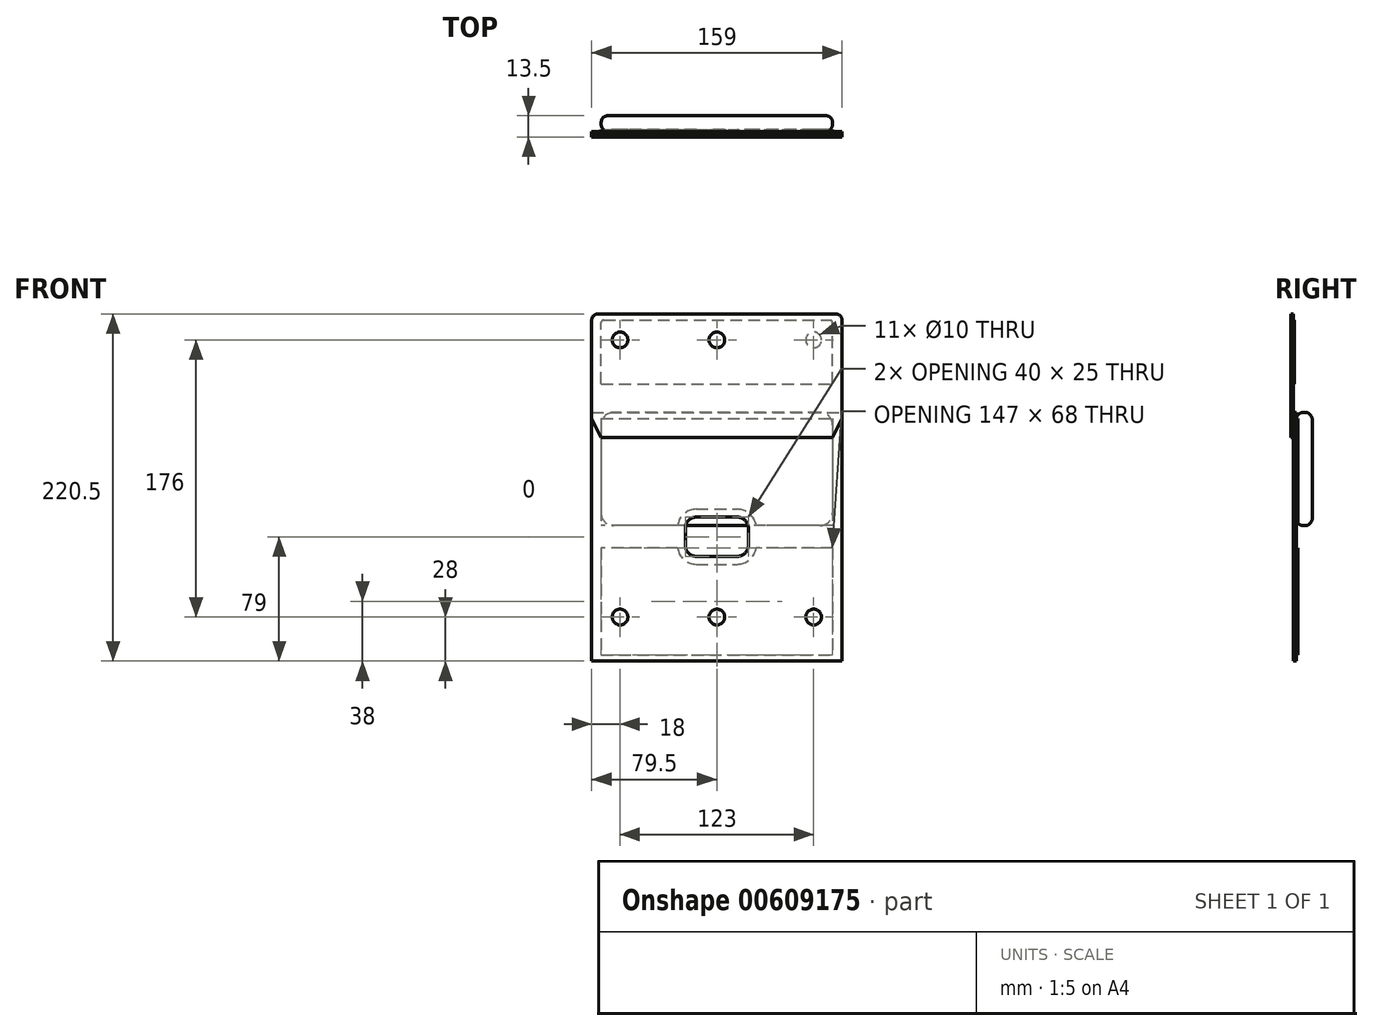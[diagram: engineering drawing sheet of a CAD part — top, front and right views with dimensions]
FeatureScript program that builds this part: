
annotation { "Feature Type Name" : "Feature", "Feature Type Description" : "" }
export const myFeature = defineFeature(function(context is Context, id is Id, definition is map)
    precondition{}
    {
        {
            var Q0;
            Q0=qCreatedBy(makeId("Front.planeOp"),FACE);
            var sketch = newSketch(context, id + "F0", { "sketchPlane" : qUnion([Q0])});
            skLineSegment(sketch, "E0.bottom", {"start": v(65.5, 36) * mm, "end": v(-65.5, 36) * mm});
            skLineSegment(sketch, "E0.top", {"start": v(65.5, -36) * mm, "end": v(-65.5, -36) * mm});
            skLineSegment(sketch, "E0.left", {"start": v(73.5, 28) * mm, "end": v(73.5, -28) * mm});
            skLineSegment(sketch, "E0.right", {"start": v(-73.5, 28) * mm, "end": v(-73.5, -28) * mm});
            skPoint(sketch, "E0.middle", {"position": v(0, 0) * mm});
            skPoint(sketch, "E1.visualSharp", {"position": v(-73.5, 36) * mm});
            skArc(sketch, "E1.filletArc", {"start": v(-65.5, 36) * mm, "mid": v(-71.16, 33.66) * mm, "end": v(-73.5, 28) * mm});
            skPoint(sketch, "E2.visualSharp", {"position": v(-73.5, -36) * mm});
            skArc(sketch, "E2.filletArc", {"start": v(-73.5, -28) * mm, "mid": v(-71.16, -33.66) * mm, "end": v(-65.5, -36) * mm});
            skPoint(sketch, "E3.visualSharp", {"position": v(73.5, -36) * mm});
            skArc(sketch, "E3.filletArc", {"start": v(65.5, -36) * mm, "mid": v(71.16, -33.66) * mm, "end": v(73.5, -28) * mm});
            skPoint(sketch, "E4.visualSharp", {"position": v(73.5, 36) * mm});
            skArc(sketch, "E4.filletArc", {"start": v(73.5, 28) * mm, "mid": v(71.16, 33.66) * mm, "end": v(65.5, 36) * mm});
            skSolve(sketch);
        }
        {
            var Q0;
            Q0=makeQuery(id+"F0.imprint","IMPRINT",FACE,{"disambiguationData":[TD([[makeQuery(id+"F0.imprint","IMPRINT",EDGE,{"derivedFrom":sQuery(id+"F0.wireOp",EDGE,"E0.bottom")}),1.0]])]});
            extrude(context, id + "F1", {"entities" : qUnion([Q0]), "endBound" : BoundingType.SYMMETRIC, "depth" : 10 * mm, "offsetDistance" : 25 * mm});
        }
        {
            var Q0;
            Q0=makeQuery(id+"F1.opExtrude","CAP_FACE",FACE,{"disambiguationData":[OSD([sQuery(id+"F0.wireOp",EDGE,"E0.bottom"),sQuery(id+"F0.wireOp",EDGE,"E0.top"),sQuery(id+"F0.wireOp",EDGE,"E0.left"),sQuery(id+"F0.wireOp",EDGE,"E0.right"),sQuery(id+"F0.wireOp",EDGE,"E1.filletArc"),sQuery(id+"F0.wireOp",EDGE,"E2.filletArc"),sQuery(id+"F0.wireOp",EDGE,"E3.filletArc"),sQuery(id+"F0.wireOp",EDGE,"E4.filletArc")])],"isStart":false});
            var Q1;
            Q1=makeQuery(id+"F1.opExtrude","CAP_FACE",FACE,{"disambiguationData":[OSD([sQuery(id+"F0.wireOp",EDGE,"E0.bottom"),sQuery(id+"F0.wireOp",EDGE,"E0.top"),sQuery(id+"F0.wireOp",EDGE,"E0.left"),sQuery(id+"F0.wireOp",EDGE,"E0.right"),sQuery(id+"F0.wireOp",EDGE,"E1.filletArc"),sQuery(id+"F0.wireOp",EDGE,"E2.filletArc"),sQuery(id+"F0.wireOp",EDGE,"E3.filletArc"),sQuery(id+"F0.wireOp",EDGE,"E4.filletArc")])],"isStart":true});
            fillet(context, id + "F2", {"entities" : qUnion([Q0, Q1]), "radius" : 4.5 * mm, "tangentPropagation" : true, "allowEdgeOverflow" : false});
        }
        {
            var Q0;
            Q0=makeQuery(id+"F1.opExtrude","CAP_FACE",FACE,{"disambiguationData":[OSD([sQuery(id+"F0.wireOp",EDGE,"E0.bottom"),sQuery(id+"F0.wireOp",EDGE,"E0.top"),sQuery(id+"F0.wireOp",EDGE,"E0.left"),sQuery(id+"F0.wireOp",EDGE,"E0.right"),sQuery(id+"F0.wireOp",EDGE,"E1.filletArc"),sQuery(id+"F0.wireOp",EDGE,"E2.filletArc"),sQuery(id+"F0.wireOp",EDGE,"E3.filletArc"),sQuery(id+"F0.wireOp",EDGE,"E4.filletArc")])],"isStart":false});
            var sketch = newSketch(context, id + "F3", { "sketchPlane" : qUnion([Q0])});
            skLineSegment(sketch, "E5.0", {"start": v(-65.5, 36) * mm, "end": v(65.5, 36) * mm});
            skLineSegment(sketch, "E6.0", {"start": v(-73.5, -122) * mm, "end": v(-73.5, 36) * mm, "construction": true});
            skLineSegment(sketch, "E7.0", {"start": v(73.5, 36) * mm, "end": v(73.5, -122) * mm, "construction": true});
            skLineSegment(sketch, "E8.0", {"start": v(73.5, -36) * mm, "end": v(24.9, -36) * mm});
            skPoint(sketch, "E9.orphan", {"position": v(-73.5, 28) * mm});
            skPoint(sketch, "E10.orphan", {"position": v(-65.5, 36) * mm});
            skPoint(sketch, "E11.orphan", {"position": v(73.5, 28) * mm});
            skPoint(sketch, "E12.orphan", {"position": v(65.5, 36) * mm});
            skLineSegment(sketch, "E13", {"start": v(-20, -43) * mm, "end": v(20, -43) * mm, "construction": true});
            skLineSegment(sketch, "E14.MirrorCS", {"start": v(-79.5, -122) * mm, "end": v(79.5, -122) * mm, "construction": true});
            skPoint(sketch, "E15.orphan", {"position": v(-73.5, -28) * mm});
            skPoint(sketch, "E16.orphan", {"position": v(73.5, -28) * mm});
            skLineSegment(sketch, "E17", {"start": v(-73.5, 32) * mm, "end": v(73.5, 32) * mm});
            skLineSegment(sketch, "E18", {"start": v(-79.5, 36) * mm, "end": v(-79.5, -122) * mm});
            skLineSegment(sketch, "E19.MirrorCS", {"start": v(79.5, 36) * mm, "end": v(79.5, -122) * mm});
            skPoint(sketch, "E20.orphan", {"position": v(79.5, 36) * mm});
            skPoint(sketch, "E21.orphan", {"position": v(0, 32) * mm});
            skPoint(sketch, "E22.orphan", {"position": v(-65.5, -36) * mm});
            skPoint(sketch, "E23.orphan", {"position": v(65.5, -36) * mm});
            skLineSegment(sketch, "E24", {"start": v(-73.5, 32) * mm, "end": v(-73.5, -36) * mm});
            skLineSegment(sketch, "E25", {"start": v(73.5, 32) * mm, "end": v(73.5, -36) * mm});
            skLineSegment(sketch, "E26.trimOffspring", {"start": v(-24.9, -36) * mm, "end": v(-73.5, -36) * mm});
            skLineSegment(sketch, "E27.MirrorCS", {"start": v(-24.9, -50) * mm, "end": v(-73.5, -50) * mm});
            skLineSegment(sketch, "E28.MirrorCS", {"start": v(-73.5, 36) * mm, "end": v(-73.5, -122) * mm, "construction": true});
            skLineSegment(sketch, "E29.MirrorCS", {"start": v(-73.5, -118) * mm, "end": v(73.5, -118) * mm});
            skLineSegment(sketch, "E30.MirrorCS", {"start": v(73.5, -50) * mm, "end": v(24.9, -50) * mm});
            skLineSegment(sketch, "E31", {"start": v(-73.5, -50) * mm, "end": v(-73.5, -118) * mm});
            skLineSegment(sketch, "E32", {"start": v(73.5, -50) * mm, "end": v(73.5, -118) * mm});
            skCircle(sketch, "E33", {"center": v(61.5, -94) * mm, "radius": 5 * mm});
            skCircle(sketch, "E34.MirrorC", {"center": v(-61.5, -94) * mm, "radius": 5 * mm});
            skLineSegment(sketch, "E35", {"start": v(79.5, 36) * mm, "end": v(-79.5, 36) * mm});
            skPoint(sketch, "E36.orphan", {"position": v(-79.5, 36) * mm});
            skLineSegment(sketch, "E37.MirrorCS", {"start": v(79.5, -122) * mm, "end": v(-79.5, -122) * mm});
            skLineSegment(sketch, "E38.bottom", {"start": v(-13, -30.5) * mm, "end": v(13, -30.5) * mm});
            skLineSegment(sketch, "E38.top", {"start": v(-13, -55.5) * mm, "end": v(13, -55.5) * mm});
            skLineSegment(sketch, "E38.left", {"start": v(-20, -37.5) * mm, "end": v(-20, -48.5) * mm});
            skLineSegment(sketch, "E38.right", {"start": v(20, -37.5) * mm, "end": v(20, -48.5) * mm});
            skPoint(sketch, "E39.visualSharp", {"position": v(-20, -30.5) * mm});
            skArc(sketch, "E39.filletArc", {"start": v(-13, -30.5) * mm, "mid": v(-17.95, -32.55) * mm, "end": v(-20, -37.5) * mm});
            skPoint(sketch, "E40.visualSharp", {"position": v(-20, -55.5) * mm});
            skArc(sketch, "E40.filletArc", {"start": v(-20, -48.5) * mm, "mid": v(-17.95, -53.45) * mm, "end": v(-13, -55.5) * mm});
            skPoint(sketch, "E41.visualSharp", {"position": v(20, -55.5) * mm});
            skArc(sketch, "E41.filletArc", {"start": v(13, -55.5) * mm, "mid": v(17.95, -53.45) * mm, "end": v(20, -48.5) * mm});
            skPoint(sketch, "E42.visualSharp", {"position": v(20, -30.5) * mm});
            skArc(sketch, "E42.filletArc", {"start": v(20, -37.5) * mm, "mid": v(17.95, -32.55) * mm, "end": v(13, -30.5) * mm});
            skArc(sketch, "E43", {"start": v(-13, -25.5) * mm, "mid": v(-20.94, -28.5) * mm, "end": v(-24.9, -36) * mm});
            skLineSegment(sketch, "E44", {"start": v(-13, -25.5) * mm, "end": v(13, -25.5) * mm});
            skPoint(sketch, "E45.orphan", {"position": v(-22.7, -36) * mm});
            skPoint(sketch, "E46.orphan", {"position": v(22.7, -36) * mm});
            skArc(sketch, "E47.MirrorCS", {"start": v(13, -25.5) * mm, "mid": v(20.94, -28.5) * mm, "end": v(24.9, -36) * mm});
            skArc(sketch, "E48.MirrorCS", {"start": v(-13, -60.5) * mm, "mid": v(-20.94, -57.5) * mm, "end": v(-24.9, -50) * mm});
            skLineSegment(sketch, "E49.MirrorCS", {"start": v(-13, -60.5) * mm, "end": v(13, -60.5) * mm});
            skArc(sketch, "E50.MirrorCS", {"start": v(13, -60.5) * mm, "mid": v(20.94, -57.5) * mm, "end": v(24.9, -50) * mm});
            skPoint(sketch, "E51.orphan", {"position": v(-22.7, -50) * mm});
            skPoint(sketch, "E52.orphan", {"position": v(22.7, -50) * mm});
            skCircle(sketch, "E53", {"center": v(0, -94) * mm, "radius": 5 * mm});
            skSolve(sketch);
        }
        {
            var Q0;
            Q0=qSketchRegion(id+"F3",true);
            var Q1;
            {var subQ10=sQuery(id+"F3.wireOp",EDGE,"E44");Q1=makeQuery(id+"F3.imprint","IMPRINT",FACE,{"disambiguationData":[TD([[makeQuery(id+"F3.imprint","IMPRINT",EDGE,{"derivedFrom":subQ10}),1.0]])]});}
            var Q2;
            Q2=makeQuery(id+"F3.imprint","IMPRINT",FACE,{"disambiguationData":[TD([[makeQuery(id+"F3.imprint","IMPRINT",EDGE,{"derivedFrom":sQuery(id+"F3.wireOp",EDGE,"E27.MirrorCS")}),1.0]])]});
            var Q3;
            {var subQ10=sQuery(id+"F3.wireOp",EDGE,"E8.0");Q3=makeQuery(id+"F3.imprint","IMPRINT",FACE,{"disambiguationData":[TD([[makeQuery(id+"F3.imprint","IMPRINT",EDGE,{"derivedFrom":subQ10}),-1.0]])]});}
            extrude(context, id + "F4", {"entities" : qUnion([Q0, Q1, Q2, Q3]), "depth" : 2 * mm, "offsetDistance" : 25 * mm});
        }
        {
            var Q0;
            {var subQ10=sQuery(id+"F3.wireOp",EDGE,"E8.0");Q0=makeQuery(id+"F3.imprint","IMPRINT",FACE,{"disambiguationData":[TD([[makeQuery(id+"F3.imprint","IMPRINT",EDGE,{"derivedFrom":subQ10}),-1.0]])]});}
            var Q1;
            {var subQ10=sQuery(id+"F3.wireOp",EDGE,"E44");Q1=makeQuery(id+"F3.imprint","IMPRINT",FACE,{"disambiguationData":[TD([[makeQuery(id+"F3.imprint","IMPRINT",EDGE,{"derivedFrom":subQ10}),1.0]])]});}
            var Q2;
            Q2=makeQuery(id+"F3.imprint","IMPRINT",FACE,{"disambiguationData":[TD([[makeQuery(id+"F3.imprint","IMPRINT",EDGE,{"derivedFrom":sQuery(id+"F3.wireOp",EDGE,"E27.MirrorCS")}),1.0]])]});
            extrude(context, id + "F5", {"entities" : qUnion([Q0, Q1, Q2]), "oppositeDirection" : true, "depth" : 1 * mm, "offsetDistance" : 25 * mm});
        }
        {
            var Q0;
            Q0=makeQuery(id+"F4.opExtrude","CAP_FACE",FACE,{"disambiguationData":[OSD([sQuery(id+"F3.wireOp",EDGE,"E18"),sQuery(id+"F3.wireOp",EDGE,"E19.MirrorCS"),sQuery(id+"F3.wireOp",EDGE,"E33"),sQuery(id+"F3.wireOp",EDGE,"E34.MirrorC"),sQuery(id+"F3.wireOp",EDGE,"E35"),sQuery(id+"F3.wireOp",EDGE,"E37.MirrorCS"),sQuery(id+"F3.wireOp",EDGE,"E38.bottom"),sQuery(id+"F3.wireOp",EDGE,"E38.top"),sQuery(id+"F3.wireOp",EDGE,"E38.left"),sQuery(id+"F3.wireOp",EDGE,"E38.right"),sQuery(id+"F3.wireOp",EDGE,"E39.filletArc"),sQuery(id+"F3.wireOp",EDGE,"E40.filletArc"),sQuery(id+"F3.wireOp",EDGE,"E41.filletArc"),sQuery(id+"F3.wireOp",EDGE,"E42.filletArc")])],"isStart":false});
            var sketch = newSketch(context, id + "F6", { "sketchPlane" : qUnion([Q0])});
            skLineSegment(sketch, "E54", {"start": v(-79.5, 94.5) * mm, "end": v(-79.5, 32) * mm});
            skLineSegment(sketch, "E55", {"start": v(-79.5, 32) * mm, "end": v(-73.5, 20.16) * mm});
            skLineSegment(sketch, "E56", {"start": v(-73.5, 20.16) * mm, "end": v(0, 20.16) * mm});
            skLineSegment(sketch, "E57", {"start": v(0, 98.5) * mm, "end": v(-75.5, 98.5) * mm});
            skLineSegment(sketch, "E58", {"start": v(-88.59, 54) * mm, "end": v(5.64, 54) * mm, "construction": true});
            skPoint(sketch, "E59.visualSharp", {"position": v(-79.5, 98.5) * mm});
            skArc(sketch, "E59.filletArc", {"start": v(-75.5, 98.5) * mm, "mid": v(-78.33, 97.32) * mm, "end": v(-79.5, 94.5) * mm});
            skLineSegment(sketch, "E60.MirrorCS", {"start": v(0, 98.5) * mm, "end": v(75.5, 98.5) * mm});
            skArc(sketch, "E61.MirrorCS", {"start": v(75.5, 98.5) * mm, "mid": v(78.33, 97.32) * mm, "end": v(79.5, 94.5) * mm});
            skLineSegment(sketch, "E62.MirrorCS", {"start": v(79.5, 94.5) * mm, "end": v(79.5, 32) * mm});
            skLineSegment(sketch, "E63.MirrorCS", {"start": v(79.5, 32) * mm, "end": v(73.5, 20.16) * mm});
            skLineSegment(sketch, "E64.MirrorCS", {"start": v(73.5, 20.16) * mm, "end": v(0, 20.16) * mm});
            skLineSegment(sketch, "E65.bottom", {"start": v(-73.5, 54) * mm, "end": v(73.5, 54) * mm});
            skLineSegment(sketch, "E65.top", {"start": v(-72, 94.5) * mm, "end": v(72, 94.5) * mm});
            skLineSegment(sketch, "E65.left", {"start": v(-73.5, 54) * mm, "end": v(-73.5, 93) * mm});
            skLineSegment(sketch, "E65.right", {"start": v(73.5, 54) * mm, "end": v(73.5, 93) * mm});
            skArc(sketch, "E66.filletArc", {"start": v(-72, 94.5) * mm, "mid": v(-73.06, 94.06) * mm, "end": v(-73.5, 93) * mm});
            skArc(sketch, "E67.filletArc", {"start": v(73.5, 93) * mm, "mid": v(73.06, 94.06) * mm, "end": v(72, 94.5) * mm});
            skCircle(sketch, "E68", {"center": v(61.5, 82) * mm, "radius": 5 * mm});
            skCircle(sketch, "E69.MirrorC", {"center": v(-61.5, 82) * mm, "radius": 5 * mm});
            skCircle(sketch, "E70", {"center": v(0, 82) * mm, "radius": 5 * mm});
            skSolve(sketch);
        }
        {
            var Q0;
            Q0=makeQuery(id+"F6.imprint","IMPRINT",FACE,{"disambiguationData":[TD([[makeQuery(id+"F6.imprint","IMPRINT",EDGE,{"derivedFrom":sQuery(id+"F6.wireOp",EDGE,"E57")}),1.0]])]});
            var Q1;
            {var subQ3=sQuery(id+"F6.wireOp",EDGE,"E55");Q1=makeQuery(id+"F6.imprint","IMPRINT",FACE,{"disambiguationData":[TD([[makeQuery(id+"F6.imprint","IMPRINT",EDGE,{"derivedFrom":subQ3}),1.0]])]});}
            var Q2;
            Q2=makeQuery(id+"F6.imprint","IMPRINT",FACE,{"disambiguationData":[TD([[makeQuery(id+"F6.imprint","IMPRINT",EDGE,{"derivedFrom":sQuery(id+"F6.wireOp",EDGE,"E65.bottom")}),1.0]])]});
            var Q3;
            Q3=makeQuery(id+"F6.imprint","IMPRINT",FACE,{"disambiguationData":[TD([[makeQuery(id+"F6.imprint","IMPRINT",EDGE,{"derivedFrom":sQuery(id+"F6.wireOp",EDGE,"E68")}),1.0]])]});
            var Q4;
            Q4=makeQuery(id+"F6.imprint","IMPRINT",FACE,{"disambiguationData":[TD([[makeQuery(id+"F6.imprint","IMPRINT",EDGE,{"derivedFrom":sQuery(id+"F6.wireOp",EDGE,"E69.MirrorC")}),-1.0]])]});
            extrude(context, id + "F7", {"entities" : qUnion([Q0, Q1, Q2, Q3, Q4]), "depth" : 1.5 * mm, "offsetDistance" : 25 * mm});
        }
        {
            var Q0;
            Q0=makeQuery(id+"F6.imprint","IMPRINT",FACE,{"disambiguationData":[TD([[makeQuery(id+"F6.imprint","IMPRINT",EDGE,{"derivedFrom":sQuery(id+"F6.wireOp",EDGE,"E65.bottom")}),1.0]])]});
            extrude(context, id + "F8", {"entities" : qUnion([Q0]), "oppositeDirection" : true, "depth" : 0.55 * mm, "offsetDistance" : 25 * mm});
        }
        {
            var Q0;
            Q0=qSketchRegion(id+"F3",true);
            var Q1;
            {var subQ10=sQuery(id+"F3.wireOp",EDGE,"E8.0");Q1=makeQuery(id+"F3.imprint","IMPRINT",FACE,{"disambiguationData":[TD([[makeQuery(id+"F3.imprint","IMPRINT",EDGE,{"derivedFrom":subQ10}),-1.0]])]});}
            var Q2;
            {var subQ10=sQuery(id+"F3.wireOp",EDGE,"E44");Q2=makeQuery(id+"F3.imprint","IMPRINT",FACE,{"disambiguationData":[TD([[makeQuery(id+"F3.imprint","IMPRINT",EDGE,{"derivedFrom":subQ10}),1.0]])]});}
            var Q3;
            Q3=makeQuery(id+"F28tSR27ECiH4KY_1.opExtrude","CAP_FACE",FACE,{"disambiguationData":[OSD([sQuery(id+"F3.wireOp",EDGE,"E27.MirrorCS"),sQuery(id+"F3.wireOp",EDGE,"E29.MirrorCS"),sQuery(id+"F3.wireOp",EDGE,"E30.MirrorCS"),sQuery(id+"F3.wireOp",EDGE,"E31"),sQuery(id+"F3.wireOp",EDGE,"E32"),sQuery(id+"F3.wireOp",EDGE,"E33"),sQuery(id+"F3.wireOp",EDGE,"E34.MirrorC"),sQuery(id+"F3.wireOp",EDGE,"E48.MirrorCS"),sQuery(id+"F3.wireOp",EDGE,"E49.MirrorCS"),sQuery(id+"F3.wireOp",EDGE,"E50.MirrorCS")])],"isStart":false});
            extrude(context, id + "F9", {"entities" : qUnion([Q0, Q1, Q2, Q3]), "depth" : 1 * mm, "offsetDistance" : 25 * mm});
        }
    });
